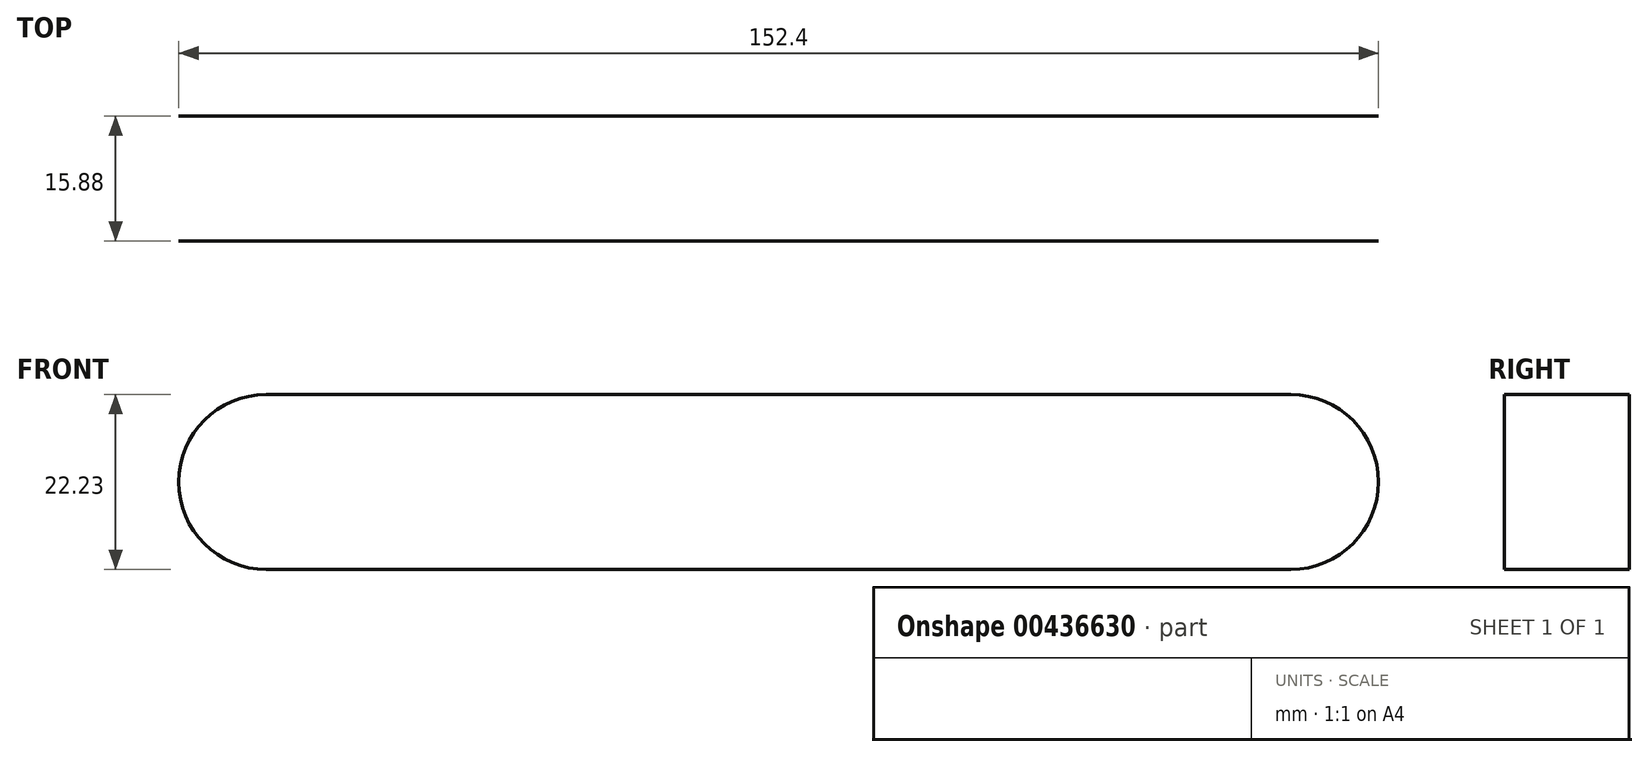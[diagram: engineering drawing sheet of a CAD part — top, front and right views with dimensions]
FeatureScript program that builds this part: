
annotation { "Feature Type Name" : "Feature", "Feature Type Description" : "" }
export const myFeature = defineFeature(function(context is Context, id is Id, definition is map)
    precondition{}
    {
        {
            var Q0;
            Q0=qCreatedBy(makeId("Front.planeOp"),FACE);
            var sketch = newSketch(context, id + "F0", { "sketchPlane" : qUnion([Q0])});
            skLineSegment(sketch, "E0.bottom", {"start": v(-30.85, 6.02) * mm, "end": v(99.32, 6.02) * mm});
            skLineSegment(sketch, "E0.top", {"start": v(-30.83, -16.2) * mm, "end": v(99.32, -16.2) * mm});
            skLineSegment(sketch, "E0.left", {"start": v(-41.96, -5.08) * mm, "end": v(-41.96, -5.1) * mm});
            skLineSegment(sketch, "E0.right", {"start": v(110.44, -5.08) * mm, "end": v(110.44, -5.1) * mm});
            skPoint(sketch, "E1.visualSharp", {"position": v(-41.96, 6.02) * mm});
            skArc(sketch, "E1.filletArc", {"start": v(-30.85, 6.02) * mm, "mid": v(-38.7, 2.76) * mm, "end": v(-41.96, -5.1) * mm});
            skPoint(sketch, "E2.visualSharp", {"position": v(-41.96, -16.2) * mm});
            skArc(sketch, "E2.filletArc", {"start": v(-41.96, -5.08) * mm, "mid": v(-38.7, -12.95) * mm, "end": v(-30.83, -16.2) * mm});
            skPoint(sketch, "E3.visualSharp", {"position": v(110.44, -16.2) * mm});
            skArc(sketch, "E3.filletArc", {"start": v(99.32, -16.2) * mm, "mid": v(107.18, -12.95) * mm, "end": v(110.44, -5.08) * mm});
            skPoint(sketch, "E4.visualSharp", {"position": v(110.44, 6.02) * mm});
            skArc(sketch, "E4.filletArc", {"start": v(110.44, -5.1) * mm, "mid": v(107.18, 2.76) * mm, "end": v(99.32, 6.02) * mm});
            skSolve(sketch);
        }
        {
            var Q0;
            {var subQ1=sQuery(id+"F0.wireOp",EDGE,"E0.bottom");Q0=makeQuery(id+"F0.imprint","IMPRINT",FACE,{"disambiguationData":[TD([[makeQuery(id+"F0.imprint","IMPRINT",EDGE,{"derivedFrom":subQ1}),-1.0]])]});}
            extrude(context, id + "F1", {"entities" : qUnion([Q0]), "depth" : 15.88 * mm, "offsetDistance" : 25.4 * mm});
        }
    });
